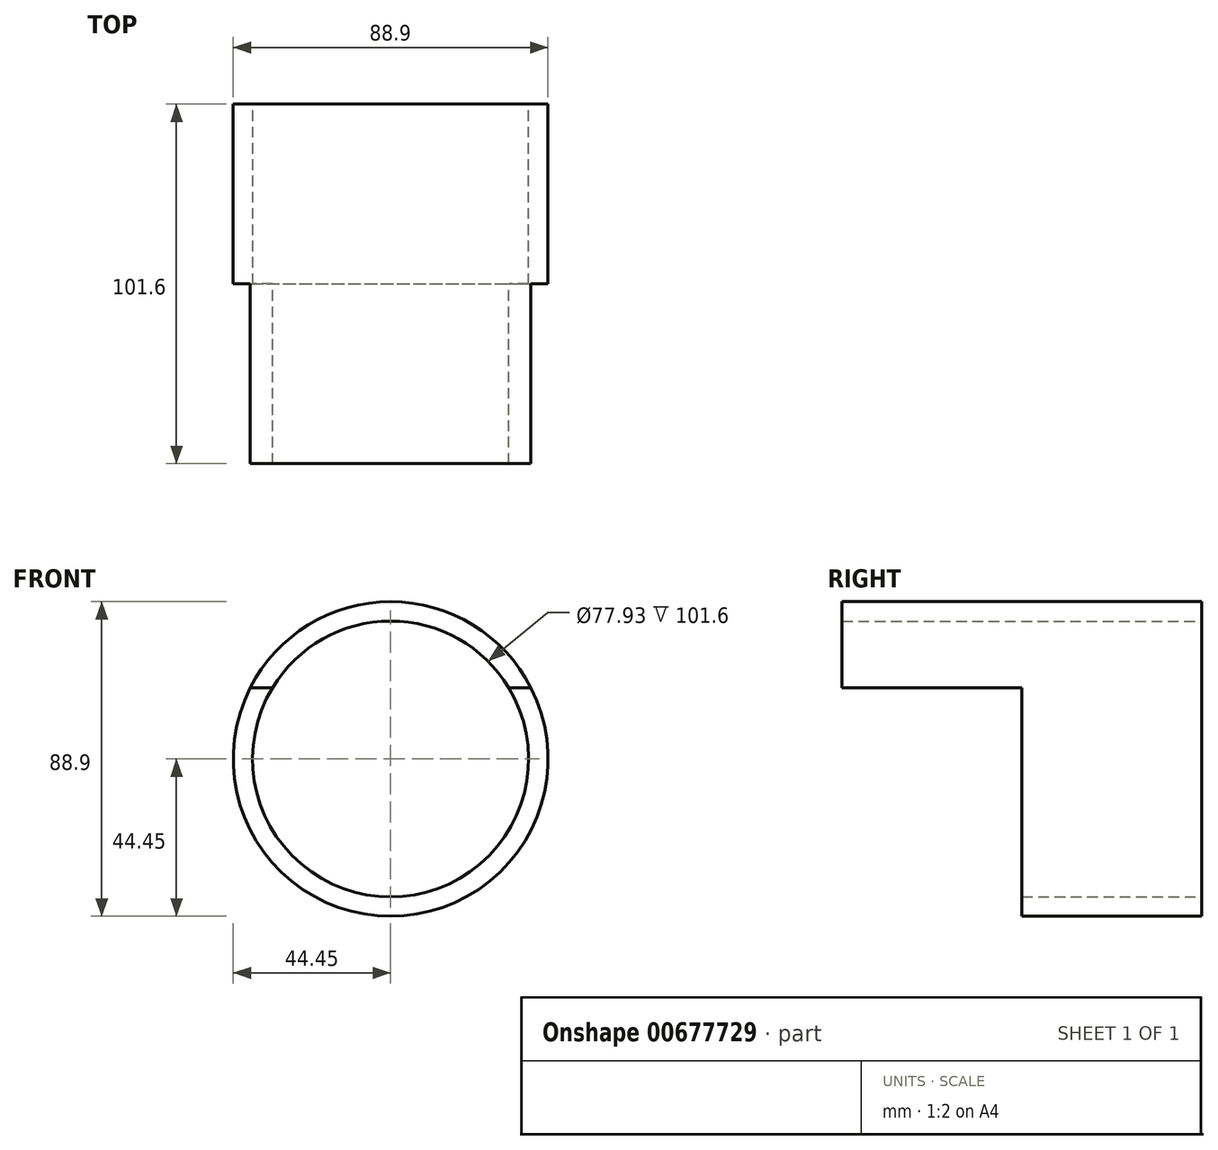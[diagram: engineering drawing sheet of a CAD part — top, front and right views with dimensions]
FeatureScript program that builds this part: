
annotation { "Feature Type Name" : "Feature", "Feature Type Description" : "" }
export const myFeature = defineFeature(function(context is Context, id is Id, definition is map)
    precondition{}
    {
        {
            var Q0;
            Q0=qCreatedBy(makeId("Front.planeOp"),FACE);
            var sketch = newSketch(context, id + "F0", { "sketchPlane" : qUnion([Q0])});
            skCircle(sketch, "E0", {"center": v(0, 0) * mm, "radius": 38.96 * mm});
            skCircle(sketch, "E1", {"center": v(0, 0) * mm, "radius": 44.45 * mm});
            skSolve(sketch);
        }
        {
            var Q0;
            Q0 = qSketchRegion(id + "F0", true);
            extrude(context, id + "F1", {"entities" : qUnion([Q0]), "depth" : 50.8 * mm, "offsetDistance" : 25.4 * mm});
        }
        {
            var Q0;
            Q0=makeQuery(id+"F1.opExtrude","CAP_FACE",FACE,{"disambiguationData":[OSD([sQuery(id+"F0.wireOp",EDGE,"E0"),sQuery(id+"F0.wireOp",EDGE,"E1")])],"isStart":false});
            var sketch = newSketch(context, id + "F2", { "sketchPlane" : qUnion([Q0])});
            skCircle(sketch, "E2.0.0", {"center": v(0, 0) * mm, "radius": 44.45 * mm});
            skLineSegment(sketch, "E3", {"start": v(-52.74, 20.15) * mm, "end": v(58.98, 20.15) * mm});
            skSolve(sketch);
        }
        {
            var Q0;
            {var subQ0=sQuery(id+"F2.wireOp",EDGE,"E3");var subQ1=sQuery(id+"F2.wireOp",EDGE,"E2.0.0");var subQ2=makeQuery(id+"F2.imprint","INTERSECT",VERTEX,{"disambiguationData":[OD(0.0)],"derivedFrom":[subQ1,subQ0]});Q0=makeQuery(id+"F2.imprint","IMPRINT",FACE,{"disambiguationData":[TD([[makeQuery(id+"F2.imprint","IMPRINT",EDGE,{"disambiguationData":[TD([[subQ2,1.0]])],"derivedFrom":subQ1}),1.0]])]});}
            extrude(context, id + "F3", {"entities" : qUnion([Q0]), "operationType" : NewBodyOperationType.ADD, "depth" : 50.8 * mm, "offsetDistance" : 25.4 * mm});
        }
    });
